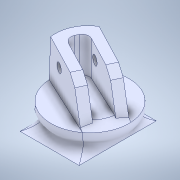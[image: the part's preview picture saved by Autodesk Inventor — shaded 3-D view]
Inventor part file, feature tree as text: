
AUTODESK INVENTOR PART (.ipt)
format: ipt  version: 2022 (Build 260153000, 153)  size: 256,000 bytes
history: mixed  units: mm
features: other x1, fillet x1, imported_body x1
ambient origin geometry x8: Origin, YZ Plane, XZ Plane, XY Plane, X Axis, Y Axis, Z Axis, Center Point
bodies: Body1 (imported_parasolid)
feature tree (3):
  other  "Sólido1"
  fillet  "Fillet1"  [1 undecoded]
  imported_body  NMx_Import_Brep_tag  [imported B-rep: ~3 faces, bbox_mm=None]
note: 1 required parameter value undecoded (feature->parameter linkage not recoverable at this tier; creation-order binding heuristic only, values carry confidence <= 0.55)
